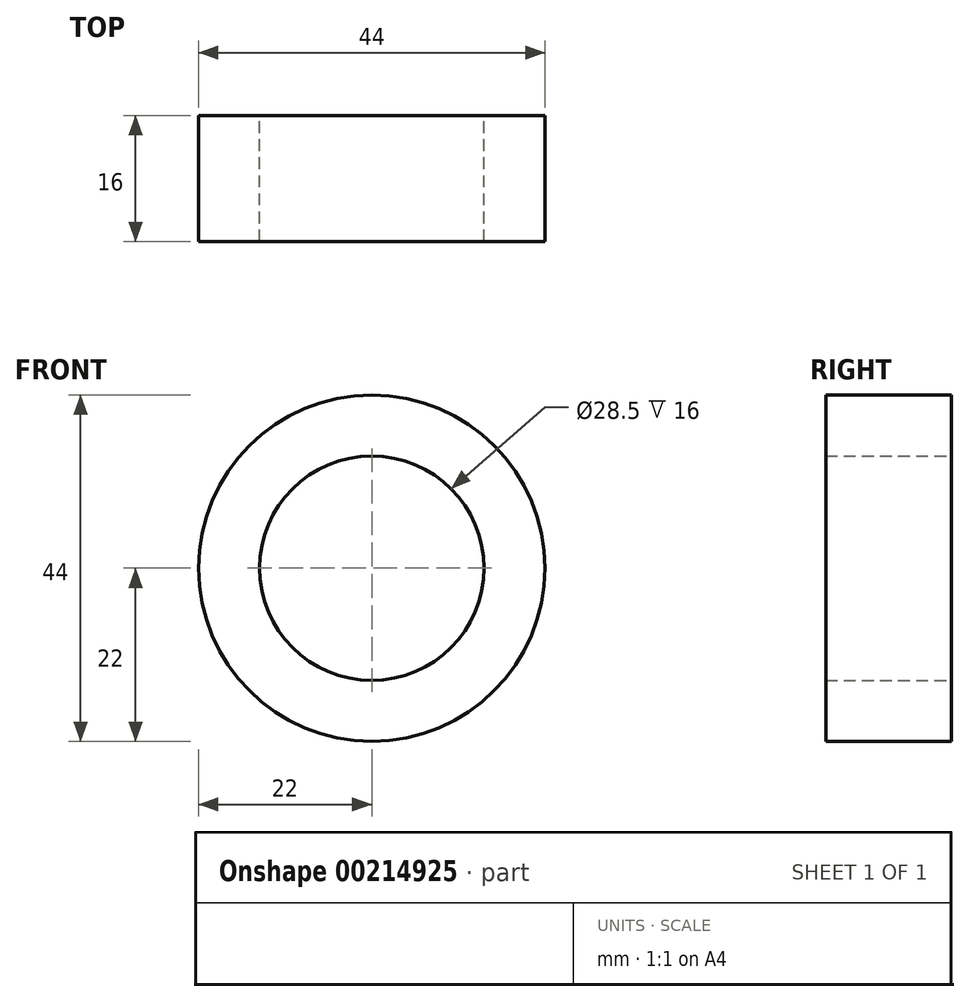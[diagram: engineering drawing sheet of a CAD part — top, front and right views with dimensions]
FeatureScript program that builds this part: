
annotation { "Feature Type Name" : "Feature", "Feature Type Description" : "" }
export const myFeature = defineFeature(function(context is Context, id is Id, definition is map)
    precondition{}
    {
        {
            var Q0;
            Q0=qCreatedBy(makeId("Front.planeOp"),FACE);
            var sketch = newSketch(context, id + "F0", { "sketchPlane" : qUnion([Q0])});
            skCircle(sketch, "E0", {"center": v(0, 0) * mm, "radius": 14.25 * mm});
            skCircle(sketch, "E1", {"center": v(0, 0) * mm, "radius": 22 * mm});
            skSolve(sketch);
        }
        {
            var Q0;
            Q0 = qSketchRegion(id + "F0", true);
            extrude(context, id + "F1", {"entities" : qUnion([Q0]), "depth" : 16 * mm, "offsetDistance" : 25 * mm});
        }
    });
